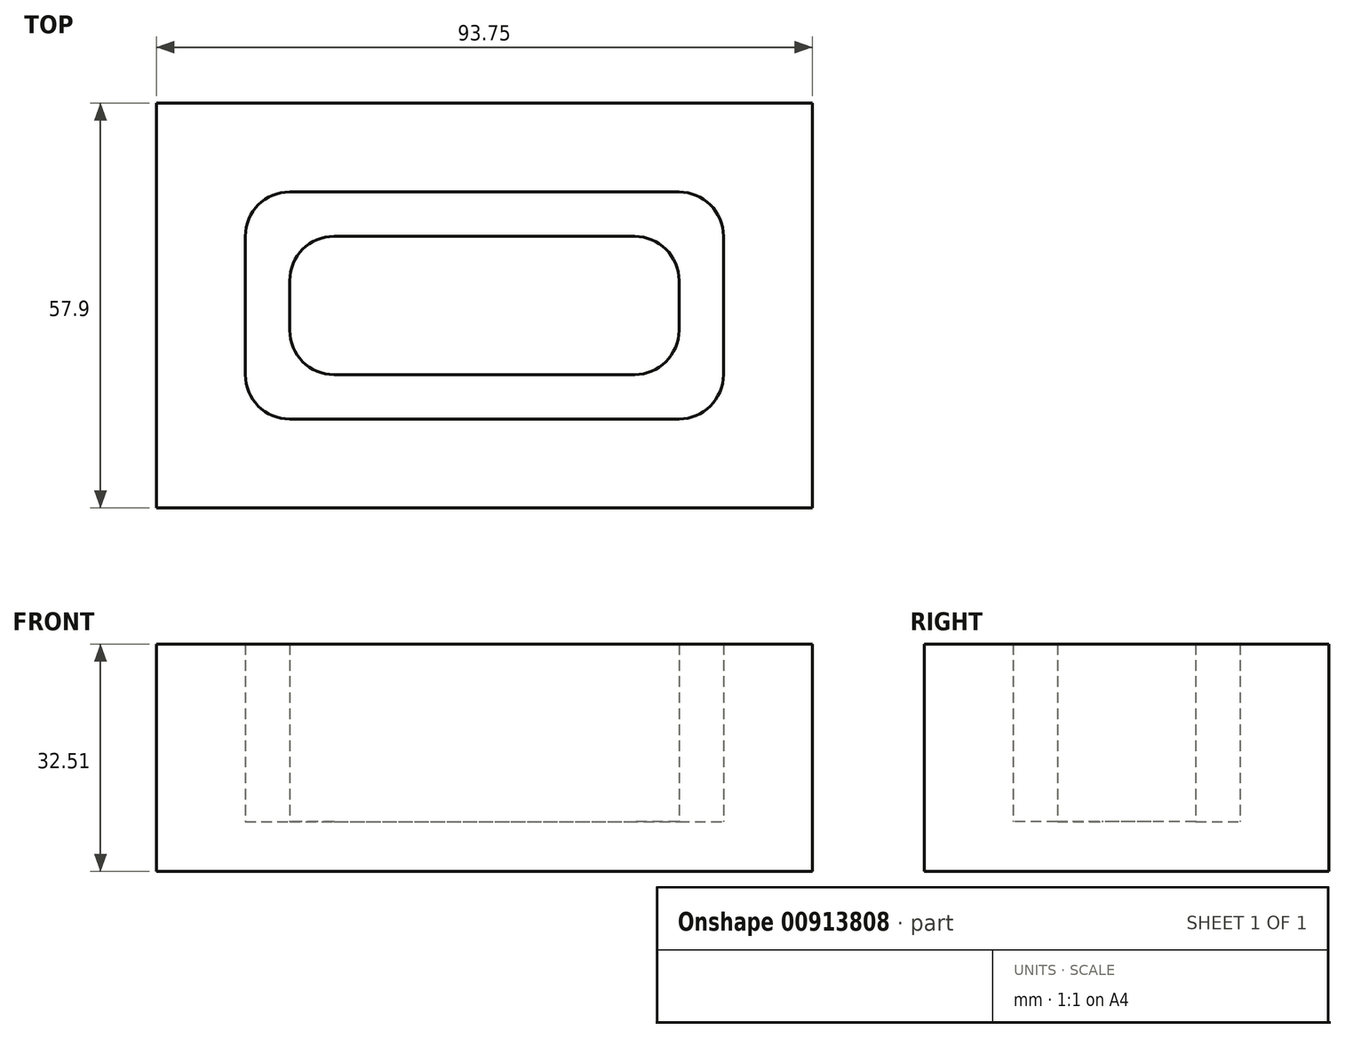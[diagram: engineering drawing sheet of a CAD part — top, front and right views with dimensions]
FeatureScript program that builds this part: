
annotation { "Feature Type Name" : "Feature", "Feature Type Description" : "" }
export const myFeature = defineFeature(function(context is Context, id is Id, definition is map)
    precondition{}
    {
        {
            var Q0;
            Q0=qCreatedBy(makeId("Top.planeOp"),FACE);
            var sketch = newSketch(context, id + "F0", { "sketchPlane" : qUnion([Q0])});
            skLineSegment(sketch, "E0.bottom", {"start": v(-35.1, 32.31) * mm, "end": v(58.65, 32.31) * mm});
            skLineSegment(sketch, "E0.top", {"start": v(-35.1, -25.59) * mm, "end": v(58.65, -25.59) * mm});
            skLineSegment(sketch, "E0.left", {"start": v(-35.1, 32.31) * mm, "end": v(-35.1, -25.59) * mm});
            skLineSegment(sketch, "E0.right", {"start": v(58.65, 32.31) * mm, "end": v(58.65, -25.59) * mm});
            skLineSegment(sketch, "E1.0", {"start": v(-16.05, -12.89) * mm, "end": v(39.6, -12.89) * mm});
            skLineSegment(sketch, "E1.1", {"start": v(-22.4, 13.26) * mm, "end": v(-22.4, -6.54) * mm});
            skLineSegment(sketch, "E1.2", {"start": v(-16.05, 19.61) * mm, "end": v(39.6, 19.61) * mm});
            skLineSegment(sketch, "E1.3", {"start": v(45.95, 13.26) * mm, "end": v(45.95, -6.54) * mm});
            skPoint(sketch, "E2.visualSharp", {"position": v(-22.4, 19.61) * mm});
            skArc(sketch, "E2.filletArc", {"start": v(-16.05, 19.61) * mm, "mid": v(-20.54, 17.75) * mm, "end": v(-22.4, 13.26) * mm});
            skPoint(sketch, "E3.visualSharp", {"position": v(-22.4, -12.89) * mm});
            skArc(sketch, "E3.filletArc", {"start": v(-22.4, -6.54) * mm, "mid": v(-20.54, -11.03) * mm, "end": v(-16.05, -12.89) * mm});
            skPoint(sketch, "E4.visualSharp", {"position": v(45.95, -12.89) * mm});
            skArc(sketch, "E4.filletArc", {"start": v(39.6, -12.89) * mm, "mid": v(44.1, -11.03) * mm, "end": v(45.95, -6.54) * mm});
            skPoint(sketch, "E5.visualSharp", {"position": v(45.95, 19.61) * mm});
            skArc(sketch, "E5.filletArc", {"start": v(45.95, 13.26) * mm, "mid": v(44.1, 17.75) * mm, "end": v(39.6, 19.61) * mm});
            skSolve(sketch);
        }
        {
            var Q0;
            Q0=makeQuery(id+"F0.imprint","IMPRINT",FACE,{"disambiguationData":[TD([[makeQuery(id+"F0.imprint","IMPRINT",EDGE,{"derivedFrom":sQuery(id+"F0.wireOp",EDGE,"E0.bottom")}),-1.0]])]});
            extrude(context, id + "F1", {"entities" : qUnion([Q0]), "depth" : 25.4 * mm, "offsetDistance" : 25.4 * mm});
        }
        {
            var Q0;
            Q0=makeQuery(id+"F1.opExtrude","CAP_FACE",FACE,{"disambiguationData":[OSD([sQuery(id+"F0.wireOp",EDGE,"E0.bottom"),sQuery(id+"F0.wireOp",EDGE,"E0.top"),sQuery(id+"F0.wireOp",EDGE,"E0.left"),sQuery(id+"F0.wireOp",EDGE,"E0.right"),sQuery(id+"F0.wireOp",EDGE,"E1.0"),sQuery(id+"F0.wireOp",EDGE,"E1.1"),sQuery(id+"F0.wireOp",EDGE,"E1.2"),sQuery(id+"F0.wireOp",EDGE,"E1.3"),sQuery(id+"F0.wireOp",EDGE,"E2.filletArc"),sQuery(id+"F0.wireOp",EDGE,"E3.filletArc"),sQuery(id+"F0.wireOp",EDGE,"E4.filletArc"),sQuery(id+"F0.wireOp",EDGE,"E5.filletArc")])],"isStart":true});
            var sketch = newSketch(context, id + "F2", { "sketchPlane" : qUnion([Q0])});
            skLineSegment(sketch, "E6.0", {"start": v(-35.1, -32.31) * mm, "end": v(-35.1, 25.59) * mm});
            skLineSegment(sketch, "E6.1", {"start": v(-35.1, 25.59) * mm, "end": v(58.65, 25.59) * mm});
            skLineSegment(sketch, "E6.2", {"start": v(58.65, -32.31) * mm, "end": v(58.65, 25.59) * mm});
            skLineSegment(sketch, "E6.3", {"start": v(-35.1, -32.31) * mm, "end": v(58.65, -32.31) * mm});
            skSolve(sketch);
        }
        {
            var Q0;
            Q0 = qSketchRegion(id + "F2", true);
            extrude(context, id + "F3", {"entities" : qUnion([Q0]), "operationType" : NewBodyOperationType.ADD, "depth" : 7.1 * mm, "offsetDistance" : 25.4 * mm});
        }
        {
            var Q0;
            Q0=makeQuery(id+"F3.opExtrude","CAP_FACE",FACE,{"disambiguationData":[OSD([sQuery(id+"F2.wireOp",EDGE,"E6.0"),sQuery(id+"F2.wireOp",EDGE,"E6.1"),sQuery(id+"F2.wireOp",EDGE,"E6.2"),sQuery(id+"F2.wireOp",EDGE,"E6.3")])],"isStart":true});
            var sketch = newSketch(context, id + "F4", { "sketchPlane" : qUnion([Q0])});
            skLineSegment(sketch, "E7.0", {"start": v(-16.05, 19.61) * mm, "end": v(39.6, 19.61) * mm});
            skLineSegment(sketch, "E7.1", {"start": v(-16.05, -12.89) * mm, "end": v(39.6, -12.89) * mm});
            skArc(sketch, "E7.2", {"start": v(-22.4, -6.54) * mm, "mid": v(-20.54, -11.03) * mm, "end": v(-16.05, -12.89) * mm});
            skPoint(sketch, "E7.3", {"position": v(-16.05, -12.89) * mm});
            skArc(sketch, "E7.4", {"start": v(39.6, -12.89) * mm, "mid": v(44.1, -11.03) * mm, "end": v(45.95, -6.54) * mm});
            skLineSegment(sketch, "E7.5", {"start": v(45.95, 13.26) * mm, "end": v(45.95, -6.54) * mm});
            skArc(sketch, "E7.6", {"start": v(-16.05, 19.61) * mm, "mid": v(-20.54, 17.75) * mm, "end": v(-22.4, 13.26) * mm});
            skLineSegment(sketch, "E7.7", {"start": v(-22.4, 13.26) * mm, "end": v(-22.4, -6.54) * mm});
            skArc(sketch, "E7.8", {"start": v(45.95, 13.26) * mm, "mid": v(44.1, 17.75) * mm, "end": v(39.6, 19.61) * mm});
            skLineSegment(sketch, "E8.0", {"start": v(-9.7, -6.54) * mm, "end": v(33.25, -6.54) * mm});
            skLineSegment(sketch, "E8.1", {"start": v(-16.05, 6.91) * mm, "end": v(-16.05, -0.19) * mm});
            skLineSegment(sketch, "E8.2", {"start": v(-9.7, 13.26) * mm, "end": v(33.25, 13.26) * mm});
            skLineSegment(sketch, "E8.3", {"start": v(39.6, 6.91) * mm, "end": v(39.6, -0.19) * mm});
            skArc(sketch, "E9.filletArc", {"start": v(39.6, 6.91) * mm, "mid": v(37.74, 11.4) * mm, "end": v(33.25, 13.26) * mm});
            skArc(sketch, "E10.filletArc", {"start": v(-9.7, 13.26) * mm, "mid": v(-14.2, 11.4) * mm, "end": v(-16.05, 6.91) * mm});
            skArc(sketch, "E11.filletArc", {"start": v(-16.05, -0.19) * mm, "mid": v(-14.2, -4.68) * mm, "end": v(-9.7, -6.54) * mm});
            skArc(sketch, "E12.filletArc", {"start": v(33.25, -6.54) * mm, "mid": v(37.74, -4.68) * mm, "end": v(39.6, -0.19) * mm});
            skSolve(sketch);
        }
        {
            var Q0;
            Q0=makeQuery(id+"F4.imprint","IMPRINT",FACE,{"disambiguationData":[TD([[makeQuery(id+"F4.imprint","IMPRINT",EDGE,{"derivedFrom":sQuery(id+"F4.wireOp",EDGE,"E8.0")}),1.0]])]});
            var sketch = newSketch(context, id + "F5", { "sketchPlane" : qUnion([Q0])});
            skSolve(sketch);
        }
        {
            var Q0;
            Q0=makeQuery(id+"F5.imprint","IMPRINT",FACE,{"disambiguationData":[TD([[makeQuery(id+"F5.imprint","IMPRINT",EDGE,{"derivedFrom":makeQuery(id+"F4.imprint","IMPRINT",EDGE,{"derivedFrom":sQuery(id+"F4.wireOp",EDGE,"E8.0")})}),1.0]])]});
            extrude(context, id + "F6", {"entities" : qUnion([Q0]), "operationType" : NewBodyOperationType.ADD, "depth" : 25.4 * mm, "offsetDistance" : 25.4 * mm});
        }
    });
